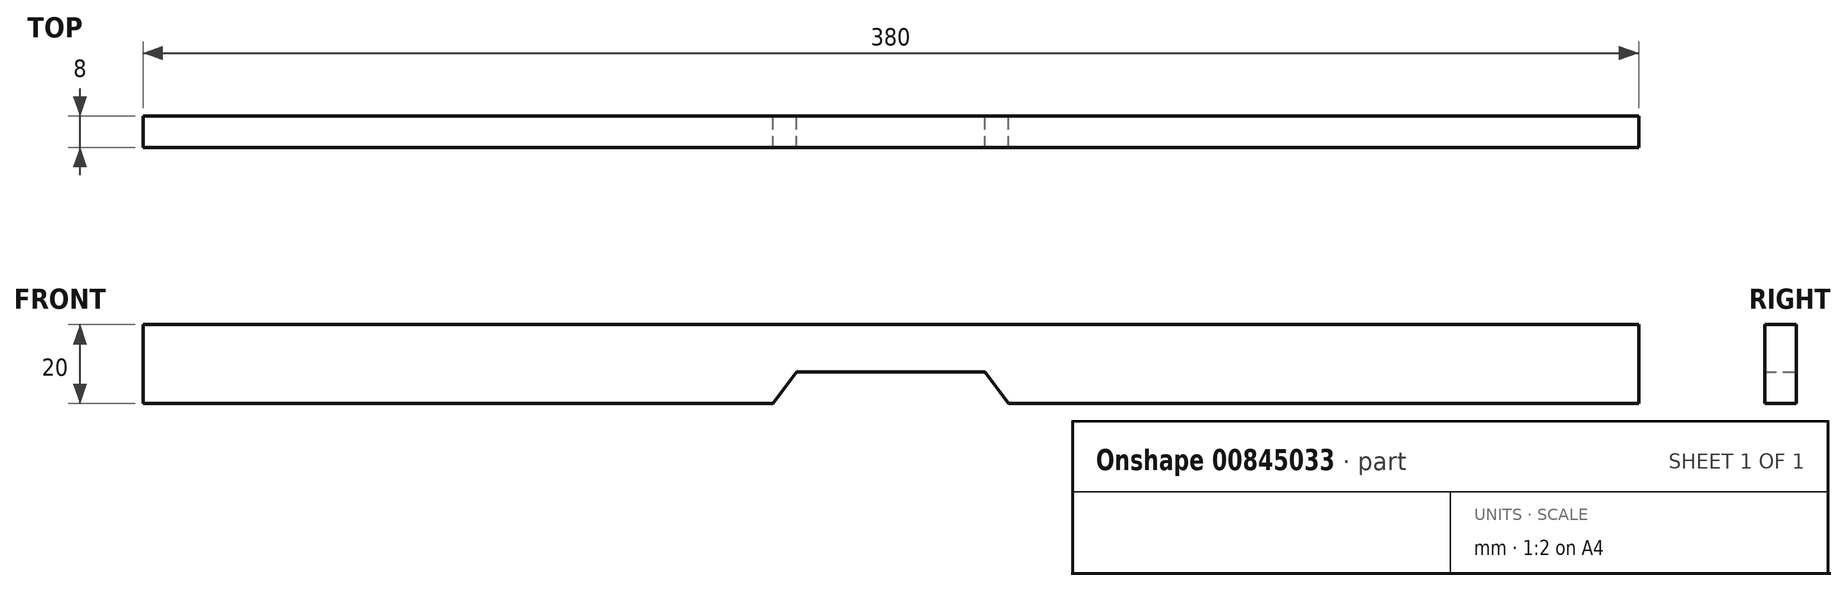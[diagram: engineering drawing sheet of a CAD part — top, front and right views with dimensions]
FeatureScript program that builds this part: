
annotation { "Feature Type Name" : "Feature", "Feature Type Description" : "" }
export const myFeature = defineFeature(function(context is Context, id is Id, definition is map)
    precondition{}
    {
        {
            var Q0;
            Q0=qCreatedBy(makeId("Front.planeOp"),FACE);
            var sketch = newSketch(context, id + "F0", { "sketchPlane" : qUnion([Q0])});
            skLineSegment(sketch, "E0.bottom", {"start": v(-190, 10) * mm, "end": v(190, 10) * mm});
            skLineSegment(sketch, "E0.top", {"start": v(-190, -10) * mm, "end": v(-29.92, -10) * mm});
            skLineSegment(sketch, "E0.left", {"start": v(-190, 10) * mm, "end": v(-190, -10) * mm});
            skLineSegment(sketch, "E0.right", {"start": v(190, 10) * mm, "end": v(190, -10) * mm});
            skPoint(sketch, "E0.middle", {"position": v(0, 0) * mm});
            skPoint(sketch, "E1", {"position": v(29.92, -10) * mm});
            skPoint(sketch, "E2", {"position": v(-29.92, -10) * mm});
            skPoint(sketch, "E3", {"position": v(-23.92, -2) * mm});
            skPoint(sketch, "E4", {"position": v(23.92, -2) * mm});
            skLineSegment(sketch, "E5", {"start": v(-23.92, -2) * mm, "end": v(23.92, -2) * mm});
            skLineSegment(sketch, "E6", {"start": v(23.92, -2) * mm, "end": v(29.92, -10) * mm});
            skLineSegment(sketch, "E7", {"start": v(-23.92, -2) * mm, "end": v(-29.92, -10) * mm});
            skLineSegment(sketch, "E8.trimOffspring", {"start": v(29.92, -10) * mm, "end": v(190, -10) * mm});
            skSolve(sketch);
        }
        {
            var Q0;
            Q0=makeQuery(id+"F0.imprint","IMPRINT",FACE,{"disambiguationData":[TD([[makeQuery(id+"F0.imprint","IMPRINT",EDGE,{"derivedFrom":sQuery(id+"F0.wireOp",EDGE,"E0.bottom")}),-1.0]])]});
            extrude(context, id + "F1", {"entities" : qUnion([Q0]), "depth" : 8 * mm, "offsetDistance" : 25 * mm});
        }
    });
